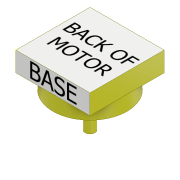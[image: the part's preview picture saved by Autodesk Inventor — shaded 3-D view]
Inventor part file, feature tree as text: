
AUTODESK INVENTOR PART (.ipt)
format: ipt  version: 2017 (Build 210142000, 142)  size: 125,952 bytes
history: native  units: mm
features: sketch x5, extrude x3
ambient origin geometry x8: Origin, YZ Plane, XZ Plane, XY Plane, X Axis, Y Axis, Z Axis, Center Point
bodies: Solid1 (feature_tree)
feature tree (8):
  extrude  "Extrusion1"  Depth=15.0mm
  extrude  "Extrusion2"  Depth=15.0mm
  extrude  "Extrusion3"  Depth=3.0mm
  sketch  "Sketch4"  dims[d8=7.0mm d9=0.0mm]
  sketch  "Sketch5"
  sketch  "Sketch1"  dims[d0=15.0mm d1=15.0mm]
  sketch  "Sketch2"  dims[d2=4.0mm d3=0.0mm d4=15.0mm]
  sketch  "Sketch3"  dims[d5=3.0mm d6=0.0mm d7=2.0mm]
